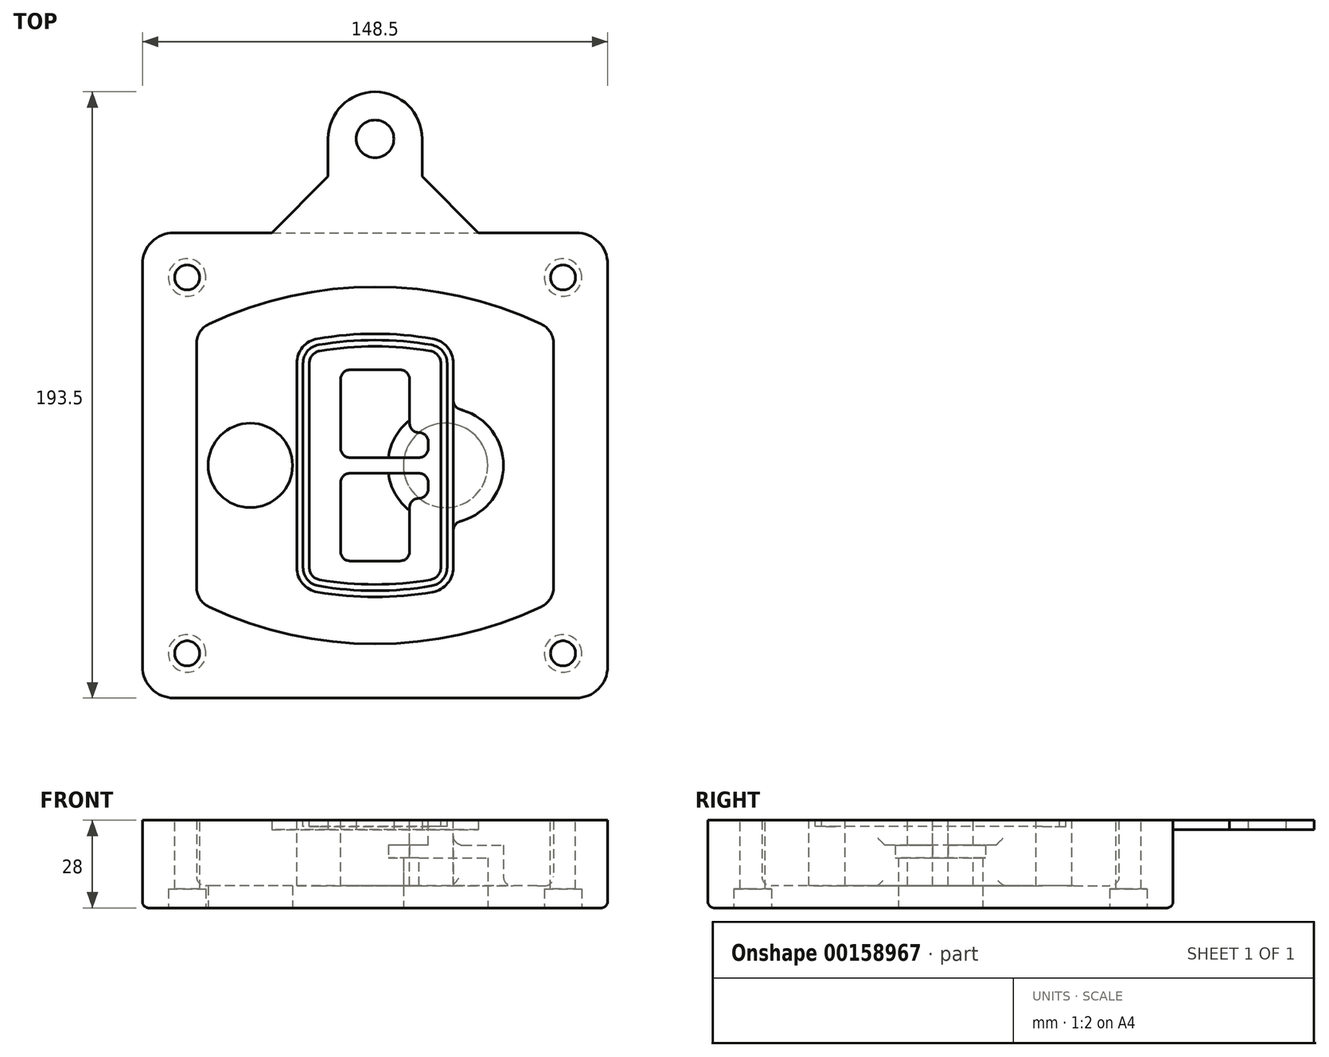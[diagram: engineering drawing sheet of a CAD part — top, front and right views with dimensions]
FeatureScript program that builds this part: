
annotation { "Feature Type Name" : "Feature", "Feature Type Description" : "" }
export const myFeature = defineFeature(function(context is Context, id is Id, definition is map)
    precondition{}
    {
        {
            var Q0;
            Q0=qCreatedBy(makeId("Top.planeOp"),FACE);
            var sketch = newSketch(context, id + "F0", { "sketchPlane" : qUnion([Q0])});
            skPoint(sketch, "E0.rect.middle", {"position": v(0, 0) * mm});
            skLineSegment(sketch, "E1.bottom", {"start": v(-64.25, -74.25) * mm, "end": v(64.25, -74.25) * mm});
            skLineSegment(sketch, "E1.top", {"start": v(-64.25, 74.25) * mm, "end": v(64.25, 74.25) * mm});
            skLineSegment(sketch, "E1.left", {"start": v(-74.25, -64.25) * mm, "end": v(-74.25, 64.25) * mm});
            skLineSegment(sketch, "E1.right", {"start": v(74.25, -64.25) * mm, "end": v(74.25, 64.25) * mm});
            skLineSegment(sketch, "E2", {"start": v(-74.25, 74.25) * mm, "end": v(74.25, -74.25) * mm, "construction": true});
            skLineSegment(sketch, "E3", {"start": v(74.25, 74.25) * mm, "end": v(-74.25, -74.25) * mm, "construction": true});
            skCircle(sketch, "E4", {"center": v(-60, 60) * mm, "radius": 4 * mm});
            skCircle(sketch, "E5", {"center": v(60, 60) * mm, "radius": 4 * mm});
            skCircle(sketch, "E6", {"center": v(60, -60) * mm, "radius": 4 * mm});
            skCircle(sketch, "E7", {"center": v(-60, -60) * mm, "radius": 4 * mm});
            skLineSegment(sketch, "E8", {"start": v(-60, 60) * mm, "end": v(60, 60) * mm, "construction": true});
            skLineSegment(sketch, "E9", {"start": v(60, 60) * mm, "end": v(60, -60) * mm, "construction": true});
            skLineSegment(sketch, "E10", {"start": v(60, -60) * mm, "end": v(-60, -60) * mm, "construction": true});
            skLineSegment(sketch, "E11", {"start": v(-60, -60) * mm, "end": v(-60, 60) * mm, "construction": true});
            skLineSegment(sketch, "E12", {"start": v(-60, 38.83) * mm, "end": v(-60, -38.83) * mm});
            skLineSegment(sketch, "E13", {"start": v(60, 38.83) * mm, "end": v(60, -38.83) * mm});
            skArc(sketch, "E14", {"start": v(54.26, 47.88) * mm, "mid": v(0, 60) * mm, "end": v(-54.26, 47.88) * mm});
            skArc(sketch, "E15", {"start": v(-54.26, -47.88) * mm, "mid": v(0, -60) * mm, "end": v(54.26, -47.88) * mm});
            skLineSegment(sketch, "E16", {"start": v(-60, 0) * mm, "end": v(60, 0) * mm, "construction": true});
            skPoint(sketch, "E17.visualSharp", {"position": v(-60, -45) * mm});
            skArc(sketch, "E17.filletArc", {"start": v(-60, -38.83) * mm, "mid": v(-58.44, -44.2) * mm, "end": v(-54.26, -47.88) * mm});
            skPoint(sketch, "E18.visualSharp", {"position": v(-60, 45) * mm});
            skArc(sketch, "E18.filletArc", {"start": v(-54.26, 47.88) * mm, "mid": v(-58.44, 44.2) * mm, "end": v(-60, 38.83) * mm});
            skPoint(sketch, "E19.visualSharp", {"position": v(60, 45) * mm});
            skArc(sketch, "E19.filletArc", {"start": v(60, 38.83) * mm, "mid": v(58.44, 44.2) * mm, "end": v(54.26, 47.88) * mm});
            skPoint(sketch, "E20.visualSharp", {"position": v(60, -45) * mm});
            skArc(sketch, "E20.filletArc", {"start": v(54.26, -47.88) * mm, "mid": v(58.44, -44.2) * mm, "end": v(60, -38.83) * mm});
            skPoint(sketch, "E21.visualSharp", {"position": v(-74.25, 74.25) * mm});
            skArc(sketch, "E21.filletArc", {"start": v(-64.25, 74.25) * mm, "mid": v(-71.32, 71.32) * mm, "end": v(-74.25, 64.25) * mm});
            skPoint(sketch, "E22.visualSharp", {"position": v(74.25, 74.25) * mm});
            skArc(sketch, "E22.filletArc", {"start": v(74.25, 64.25) * mm, "mid": v(71.32, 71.32) * mm, "end": v(64.25, 74.25) * mm});
            skPoint(sketch, "E23.visualSharp", {"position": v(74.25, -74.25) * mm});
            skArc(sketch, "E23.filletArc", {"start": v(64.25, -74.25) * mm, "mid": v(71.32, -71.32) * mm, "end": v(74.25, -64.25) * mm});
            skPoint(sketch, "E24.visualSharp", {"position": v(-74.25, -74.25) * mm});
            skArc(sketch, "E24.filletArc", {"start": v(-74.25, -64.25) * mm, "mid": v(-71.32, -71.32) * mm, "end": v(-64.25, -74.25) * mm});
            skArc(sketch, "E25.0", {"start": v(57, 38.83) * mm, "mid": v(55.9, 42.58) * mm, "end": v(52.98, 45.17) * mm});
            skLineSegment(sketch, "E25.1", {"start": v(57, 38.83) * mm, "end": v(57, -38.83) * mm});
            skArc(sketch, "E25.2", {"start": v(52.98, -45.17) * mm, "mid": v(55.9, -42.58) * mm, "end": v(57, -38.83) * mm});
            skArc(sketch, "E25.3", {"start": v(-52.98, -45.17) * mm, "mid": v(0, -57) * mm, "end": v(52.98, -45.17) * mm});
            skArc(sketch, "E25.4", {"start": v(-57, -38.83) * mm, "mid": v(-55.9, -42.58) * mm, "end": v(-52.98, -45.17) * mm});
            skArc(sketch, "E25.5", {"start": v(52.98, 45.17) * mm, "mid": v(0, 57) * mm, "end": v(-52.98, 45.17) * mm});
            skLineSegment(sketch, "E25.6", {"start": v(-57, 38.83) * mm, "end": v(-57, -38.83) * mm});
            skArc(sketch, "E25.7", {"start": v(-52.98, 45.17) * mm, "mid": v(-55.9, 42.58) * mm, "end": v(-57, 38.83) * mm});
            skArc(sketch, "E26.0", {"start": v(-55.96, 51.5) * mm, "mid": v(-61.82, 46.33) * mm, "end": v(-64, 38.83) * mm});
            skArc(sketch, "E26.1", {"start": v(55.96, 51.5) * mm, "mid": v(0, 64) * mm, "end": v(-55.96, 51.5) * mm});
            skArc(sketch, "E26.2", {"start": v(64, 38.83) * mm, "mid": v(61.82, 46.33) * mm, "end": v(55.96, 51.5) * mm});
            skLineSegment(sketch, "E26.3", {"start": v(64, 38.83) * mm, "end": v(64, -38.83) * mm});
            skArc(sketch, "E26.4", {"start": v(55.96, -51.5) * mm, "mid": v(61.82, -46.33) * mm, "end": v(64, -38.83) * mm});
            skLineSegment(sketch, "E26.5", {"start": v(-64, 38.83) * mm, "end": v(-64, -38.83) * mm});
            skArc(sketch, "E26.6", {"start": v(-55.96, -51.5) * mm, "mid": v(0, -64) * mm, "end": v(55.96, -51.5) * mm});
            skArc(sketch, "E26.7", {"start": v(-64, -38.83) * mm, "mid": v(-61.82, -46.33) * mm, "end": v(-55.96, -51.5) * mm});
            skSolve(sketch);
        }
        {
            var Q0;
            Q0=makeQuery(id+"F0.imprint","IMPRINT",FACE,{"disambiguationData":[TD([[makeQuery(id+"F0.imprint","IMPRINT",EDGE,{"derivedFrom":sQuery(id+"F0.wireOp",EDGE,"E1.bottom")}),1.0]])]});
            var Q1;
            Q1=makeQuery(id+"F0.imprint","IMPRINT",FACE,{"disambiguationData":[TD([[makeQuery(id+"F0.imprint","IMPRINT",EDGE,{"derivedFrom":sQuery(id+"F0.wireOp",EDGE,"E12")}),1.0]])]});
            var Q2;
            Q2=makeQuery(id+"F0.imprint","IMPRINT",FACE,{"disambiguationData":[TD([[makeQuery(id+"F0.imprint","IMPRINT",EDGE,{"derivedFrom":sQuery(id+"F0.wireOp",EDGE,"E25.0")}),1.0]])]});
            var Q3;
            Q3=makeQuery(id+"F0.imprint","IMPRINT",FACE,{"disambiguationData":[TD([[makeQuery(id+"F0.imprint","IMPRINT",EDGE,{"derivedFrom":sQuery(id+"F0.wireOp",EDGE,"E12")}),-1.0]])]});
            extrude(context, id + "F1", {"entities" : qUnion([Q0, Q1, Q2, Q3]), "oppositeDirection" : true, "depth" : 25 * mm});
        }
        {
            var Q0;
            Q0=makeQuery(id+"F0.imprint","IMPRINT",FACE,{"disambiguationData":[TD([[makeQuery(id+"F0.imprint","IMPRINT",EDGE,{"derivedFrom":sQuery(id+"F0.wireOp",EDGE,"E12")}),1.0]])]});
            extrude(context, id + "F2", {"entities" : qUnion([Q0]), "operationType" : NewBodyOperationType.ADD, "depth" : 3 * mm});
        }
        {
            var Q0;
            Q0=makeQuery(id+"F0.imprint","IMPRINT",FACE,{"disambiguationData":[TD([[makeQuery(id+"F0.imprint","IMPRINT",EDGE,{"derivedFrom":sQuery(id+"F0.wireOp",EDGE,"E25.0")}),1.0]])]});
            extrude(context, id + "F3", {"entities" : qUnion([Q0]), "operationType" : NewBodyOperationType.REMOVE, "oppositeDirection" : true, "depth" : 18 * mm});
        }
        {
            var Q0;
            Q0=makeQuery(id+"F2.opExtrude","CAP_FACE",FACE,{"disambiguationData":[OSD([sQuery(id+"F0.wireOp",EDGE,"E12"),sQuery(id+"F0.wireOp",EDGE,"E13"),sQuery(id+"F0.wireOp",EDGE,"E14"),sQuery(id+"F0.wireOp",EDGE,"E15"),sQuery(id+"F0.wireOp",EDGE,"E17.filletArc"),sQuery(id+"F0.wireOp",EDGE,"E18.filletArc"),sQuery(id+"F0.wireOp",EDGE,"E19.filletArc"),sQuery(id+"F0.wireOp",EDGE,"E20.filletArc"),sQuery(id+"F0.wireOp",EDGE,"E25.0"),sQuery(id+"F0.wireOp",EDGE,"E25.1"),sQuery(id+"F0.wireOp",EDGE,"E25.2"),sQuery(id+"F0.wireOp",EDGE,"E25.3"),sQuery(id+"F0.wireOp",EDGE,"E25.4"),sQuery(id+"F0.wireOp",EDGE,"E25.5"),sQuery(id+"F0.wireOp",EDGE,"E25.6"),sQuery(id+"F0.wireOp",EDGE,"E25.7")])],"isStart":false});
            var sketch = newSketch(context, id + "F4", { "sketchPlane" : qUnion([Q0])});
            skArc(sketch, "E27.0", {"start": v(-18.34, -40.45) * mm, "mid": v(0, -42) * mm, "end": v(18.34, -40.45) * mm});
            skArc(sketch, "E28.0", {"start": v(18.34, 40.45) * mm, "mid": v(0, 42) * mm, "end": v(-18.34, 40.45) * mm});
            skLineSegment(sketch, "E29", {"start": v(-25, 32.57) * mm, "end": v(-25, -32.57) * mm});
            skLineSegment(sketch, "E30", {"start": v(25, 32.57) * mm, "end": v(25, -32.57) * mm});
            skLineSegment(sketch, "E31", {"start": v(-25, 39.1) * mm, "end": v(25, 39.1) * mm, "construction": true});
            skLineSegment(sketch, "E32", {"start": v(-25, -39.1) * mm, "end": v(25, -39.1) * mm, "construction": true});
            skPoint(sketch, "E33.visualSharp", {"position": v(-25, 39.1) * mm});
            skArc(sketch, "E33.filletArc", {"start": v(-18.34, 40.45) * mm, "mid": v(-23.11, 37.73) * mm, "end": v(-25, 32.57) * mm});
            skPoint(sketch, "E34.visualSharp", {"position": v(25, 39.1) * mm});
            skArc(sketch, "E34.filletArc", {"start": v(25, 32.57) * mm, "mid": v(23.11, 37.73) * mm, "end": v(18.34, 40.45) * mm});
            skPoint(sketch, "E35.visualSharp", {"position": v(25, -39.1) * mm});
            skArc(sketch, "E35.filletArc", {"start": v(18.34, -40.45) * mm, "mid": v(23.11, -37.73) * mm, "end": v(25, -32.57) * mm});
            skPoint(sketch, "E36.visualSharp", {"position": v(-25, -39.1) * mm});
            skArc(sketch, "E36.filletArc", {"start": v(-25, -32.57) * mm, "mid": v(-23.11, -37.73) * mm, "end": v(-18.34, -40.45) * mm});
            skArc(sketch, "E37.0", {"start": v(52.98, 45.17) * mm, "mid": v(0, 57) * mm, "end": v(-52.98, 45.17) * mm});
            skArc(sketch, "E37.1", {"start": v(-52.98, 45.17) * mm, "mid": v(-55.9, 42.58) * mm, "end": v(-57, 38.83) * mm});
            skLineSegment(sketch, "E37.2", {"start": v(-57, 38.83) * mm, "end": v(-57, -38.83) * mm});
            skArc(sketch, "E37.3", {"start": v(-57, -38.83) * mm, "mid": v(-55.9, -42.58) * mm, "end": v(-52.98, -45.17) * mm});
            skArc(sketch, "E37.4", {"start": v(-52.98, -45.17) * mm, "mid": v(0, -57) * mm, "end": v(52.98, -45.17) * mm});
            skArc(sketch, "E37.5", {"start": v(52.98, -45.17) * mm, "mid": v(55.9, -42.58) * mm, "end": v(57, -38.83) * mm});
            skLineSegment(sketch, "E37.6", {"start": v(57, 38.83) * mm, "end": v(57, -38.83) * mm});
            skArc(sketch, "E37.7", {"start": v(57, 38.83) * mm, "mid": v(55.9, 42.58) * mm, "end": v(52.98, 45.17) * mm});
            skLineSegment(sketch, "E38.0", {"start": v(23, 32.57) * mm, "end": v(23, -32.57) * mm});
            skArc(sketch, "E38.1", {"start": v(18, -38.48) * mm, "mid": v(21.58, -36.44) * mm, "end": v(23, -32.57) * mm});
            skArc(sketch, "E38.2", {"start": v(-18, -38.48) * mm, "mid": v(0, -40) * mm, "end": v(18, -38.48) * mm});
            skArc(sketch, "E38.3", {"start": v(-23, -32.57) * mm, "mid": v(-21.58, -36.44) * mm, "end": v(-18, -38.48) * mm});
            skLineSegment(sketch, "E38.4", {"start": v(-23, 32.57) * mm, "end": v(-23, -32.57) * mm});
            skArc(sketch, "E38.5", {"start": v(23, 32.57) * mm, "mid": v(21.58, 36.44) * mm, "end": v(18, 38.48) * mm});
            skArc(sketch, "E38.6", {"start": v(-18, 38.48) * mm, "mid": v(-21.58, 36.44) * mm, "end": v(-23, 32.57) * mm});
            skArc(sketch, "E38.7", {"start": v(18, 38.48) * mm, "mid": v(0, 40) * mm, "end": v(-18, 38.48) * mm});
            skArc(sketch, "E39.0", {"start": v(21, 32.57) * mm, "mid": v(20.06, 35.15) * mm, "end": v(17.67, 36.5) * mm});
            skLineSegment(sketch, "E39.1", {"start": v(21, 32.57) * mm, "end": v(21, -32.57) * mm});
            skArc(sketch, "E39.2", {"start": v(17.67, -36.5) * mm, "mid": v(20.06, -35.15) * mm, "end": v(21, -32.57) * mm});
            skArc(sketch, "E39.3", {"start": v(-17.67, -36.5) * mm, "mid": v(0, -38) * mm, "end": v(17.67, -36.5) * mm});
            skArc(sketch, "E39.4", {"start": v(-21, -32.57) * mm, "mid": v(-20.06, -35.15) * mm, "end": v(-17.67, -36.5) * mm});
            skArc(sketch, "E39.5", {"start": v(17.67, 36.5) * mm, "mid": v(0, 38) * mm, "end": v(-17.67, 36.5) * mm});
            skLineSegment(sketch, "E39.6", {"start": v(-21, 32.57) * mm, "end": v(-21, -32.57) * mm});
            skArc(sketch, "E39.7", {"start": v(-17.67, 36.5) * mm, "mid": v(-20.06, 35.15) * mm, "end": v(-21, 32.57) * mm});
            skLineSegment(sketch, "E40", {"start": v(-25, 0) * mm, "end": v(25, 0) * mm, "construction": true});
            skLineSegment(sketch, "E41", {"start": v(-11, 5.5) * mm, "end": v(-11, 27.5) * mm});
            skLineSegment(sketch, "E42", {"start": v(-8, 30.5) * mm, "end": v(8, 30.5) * mm});
            skLineSegment(sketch, "E43", {"start": v(11, 27.5) * mm, "end": v(11, 13.5) * mm});
            skLineSegment(sketch, "E44", {"start": v(14, 10.5) * mm, "end": v(14, 10.5) * mm});
            skLineSegment(sketch, "E45", {"start": v(17, 7.5) * mm, "end": v(17, 5.5) * mm});
            skLineSegment(sketch, "E46", {"start": v(14, 2.5) * mm, "end": v(-8, 2.5) * mm});
            skPoint(sketch, "E47.visualSharp", {"position": v(-11, 30.5) * mm});
            skArc(sketch, "E47.filletArc", {"start": v(-8, 30.5) * mm, "mid": v(-10.12, 29.62) * mm, "end": v(-11, 27.5) * mm});
            skPoint(sketch, "E48.visualSharp", {"position": v(11, 30.5) * mm});
            skArc(sketch, "E48.filletArc", {"start": v(11, 27.5) * mm, "mid": v(10.12, 29.62) * mm, "end": v(8, 30.5) * mm});
            skPoint(sketch, "E49.visualSharp", {"position": v(11, 10.5) * mm});
            skArc(sketch, "E49.filletArc", {"start": v(11, 13.5) * mm, "mid": v(11.88, 11.38) * mm, "end": v(14, 10.5) * mm});
            skPoint(sketch, "E50.visualSharp", {"position": v(17, 10.5) * mm});
            skArc(sketch, "E50.filletArc", {"start": v(17, 7.5) * mm, "mid": v(16.12, 9.62) * mm, "end": v(14, 10.5) * mm});
            skPoint(sketch, "E51.visualSharp", {"position": v(17, 2.5) * mm});
            skArc(sketch, "E51.filletArc", {"start": v(14, 2.5) * mm, "mid": v(16.12, 3.38) * mm, "end": v(17, 5.5) * mm});
            skPoint(sketch, "E52.visualSharp", {"position": v(-11, 2.5) * mm});
            skArc(sketch, "E52.filletArc", {"start": v(-11, 5.5) * mm, "mid": v(-10.12, 3.38) * mm, "end": v(-8, 2.5) * mm});
            skLineSegment(sketch, "E53.0.MirrorCS", {"start": v(14, -2.5) * mm, "end": v(-8, -2.5) * mm});
            skArc(sketch, "E54.0.MirrorCS", {"start": v(-11, -5.5) * mm, "mid": v(-10.12, -3.38) * mm, "end": v(-8, -2.5) * mm});
            skLineSegment(sketch, "E55.0.MirrorCS", {"start": v(-11, -5.5) * mm, "end": v(-11, -27.5) * mm});
            skArc(sketch, "E56.0.MirrorCS", {"start": v(-8, -30.5) * mm, "mid": v(-10.12, -29.62) * mm, "end": v(-11, -27.5) * mm});
            skLineSegment(sketch, "E57.0.MirrorCS", {"start": v(-8, -30.5) * mm, "end": v(8, -30.5) * mm});
            skArc(sketch, "E58.0.MirrorCS", {"start": v(11, -27.5) * mm, "mid": v(10.12, -29.62) * mm, "end": v(8, -30.5) * mm});
            skLineSegment(sketch, "E59.0.MirrorCS", {"start": v(11, -27.5) * mm, "end": v(11, -13.5) * mm});
            skArc(sketch, "E60.0.MirrorCS", {"start": v(11, -13.5) * mm, "mid": v(11.88, -11.38) * mm, "end": v(14, -10.5) * mm});
            skArc(sketch, "E61.0.MirrorCS", {"start": v(17, -7.5) * mm, "mid": v(16.12, -9.62) * mm, "end": v(14, -10.5) * mm});
            skLineSegment(sketch, "E62.0.MirrorCS", {"start": v(17, -7.5) * mm, "end": v(17, -5.5) * mm});
            skArc(sketch, "E63.0.MirrorCS", {"start": v(14, -2.5) * mm, "mid": v(16.12, -3.38) * mm, "end": v(17, -5.5) * mm});
            skSolve(sketch);
        }
        {
            var Q0;
            Q0=makeQuery(id+"F4.imprint","IMPRINT",FACE,{"disambiguationData":[TD([[makeQuery(id+"F4.imprint","IMPRINT",EDGE,{"derivedFrom":sQuery(id+"F4.wireOp",EDGE,"E27.0")}),1.0]])]});
            var Q1;
            Q1=makeQuery(id+"F4.imprint","IMPRINT",FACE,{"disambiguationData":[TD([[makeQuery(id+"F4.imprint","IMPRINT",EDGE,{"derivedFrom":sQuery(id+"F4.wireOp",EDGE,"E38.0")}),-1.0]])]});
            var Q2;
            Q2=makeQuery(id+"F4.imprint","IMPRINT",FACE,{"disambiguationData":[TD([[makeQuery(id+"F4.imprint","IMPRINT",EDGE,{"derivedFrom":sQuery(id+"F4.wireOp",EDGE,"E39.0")}),1.0]])]});
            extrude(context, id + "F5", {"entities" : qUnion([Q0, Q1, Q2]), "operationType" : NewBodyOperationType.ADD, "endBound" : BoundingType.UP_TO_NEXT, "oppositeDirection" : true, "depth" : 25 * mm});
        }
        {
            var Q0;
            Q0=makeQuery(id+"F4.imprint","IMPRINT",FACE,{"disambiguationData":[TD([[makeQuery(id+"F4.imprint","IMPRINT",EDGE,{"derivedFrom":sQuery(id+"F4.wireOp",EDGE,"E38.0")}),-1.0]])]});
            extrude(context, id + "F6", {"entities" : qUnion([Q0]), "operationType" : NewBodyOperationType.REMOVE, "oppositeDirection" : true, "depth" : 2 * mm});
        }
        {
            var Q0;
            Q0=makeQuery(id+"F1.opExtrude","CAP_FACE",FACE,{"disambiguationData":[OSD([sQuery(id+"F0.wireOp",EDGE,"E1.bottom"),sQuery(id+"F0.wireOp",EDGE,"E1.top"),sQuery(id+"F0.wireOp",EDGE,"E1.left"),sQuery(id+"F0.wireOp",EDGE,"E1.right"),sQuery(id+"F0.wireOp",EDGE,"E4"),sQuery(id+"F0.wireOp",EDGE,"E5"),sQuery(id+"F0.wireOp",EDGE,"E6"),sQuery(id+"F0.wireOp",EDGE,"E7"),sQuery(id+"F0.wireOp",EDGE,"E21.filletArc"),sQuery(id+"F0.wireOp",EDGE,"E22.filletArc"),sQuery(id+"F0.wireOp",EDGE,"E23.filletArc"),sQuery(id+"F0.wireOp",EDGE,"E24.filletArc")])],"isStart":false});
            var sketch = newSketch(context, id + "F7", { "sketchPlane" : qUnion([Q0])});
            skCircle(sketch, "E64", {"center": v(22.5, 0) * mm, "radius": 13.47 * mm});
            skCircle(sketch, "E65", {"center": v(-39.81, 0) * mm, "radius": 13.47 * mm});
            skLineSegment(sketch, "E66", {"start": v(74.25, 0) * mm, "end": v(-74.25, 0) * mm});
            skCircle(sketch, "E67", {"center": v(22.5, 0) * mm, "radius": 18.47 * mm});
            skCircle(sketch, "E68", {"center": v(60, -60) * mm, "radius": 6 * mm});
            skCircle(sketch, "E69", {"center": v(-60, -60) * mm, "radius": 6 * mm});
            skCircle(sketch, "E70", {"center": v(-60, 60) * mm, "radius": 6 * mm});
            skCircle(sketch, "E71", {"center": v(60, 60) * mm, "radius": 6 * mm});
            skSolve(sketch);
        }
        {
            var Q0;
            {var subQ1=sQuery(id+"F7.wireOp",EDGE,"E66");var subQ4=sQuery(id+"F7.wireOp",EDGE,"E64");var subQ6=makeQuery(id+"F7.imprint","INTERSECT",VERTEX,{"disambiguationData":[OD(0.0)],"derivedFrom":[subQ4,subQ1]});Q0=makeQuery(id+"F7.imprint","IMPRINT",FACE,{"disambiguationData":[TD([[makeQuery(id+"F7.imprint","IMPRINT",EDGE,{"disambiguationData":[TD([[subQ6,-1.0]])],"derivedFrom":subQ4}),-1.0]])]});}
            var Q1;
            {var subQ0=sQuery(id+"F7.wireOp",EDGE,"E66");var subQ1=sQuery(id+"F7.wireOp",EDGE,"E64");var subQ3=makeQuery(id+"F7.imprint","INTERSECT",VERTEX,{"disambiguationData":[OD(0.0)],"derivedFrom":[subQ1,subQ0]});Q1=makeQuery(id+"F7.imprint","IMPRINT",FACE,{"disambiguationData":[TD([[makeQuery(id+"F7.imprint","IMPRINT",EDGE,{"disambiguationData":[TD([[subQ3,-1.0]])],"derivedFrom":subQ1}),1.0]])]});}
            var Q2;
            {var subQ0=sQuery(id+"F7.wireOp",EDGE,"E66");var subQ1=sQuery(id+"F7.wireOp",EDGE,"E64");var subQ3=makeQuery(id+"F7.imprint","INTERSECT",VERTEX,{"disambiguationData":[OD(0.0)],"derivedFrom":[subQ1,subQ0]});Q2=makeQuery(id+"F7.imprint","IMPRINT",FACE,{"disambiguationData":[TD([[makeQuery(id+"F7.imprint","IMPRINT",EDGE,{"disambiguationData":[TD([[subQ3,1.0]])],"derivedFrom":subQ1}),1.0]])]});}
            var Q3;
            {var subQ1=sQuery(id+"F7.wireOp",EDGE,"E66");var subQ4=sQuery(id+"F7.wireOp",EDGE,"E64");var subQ6=makeQuery(id+"F7.imprint","INTERSECT",VERTEX,{"disambiguationData":[OD(0.0)],"derivedFrom":[subQ4,subQ1]});Q3=makeQuery(id+"F7.imprint","IMPRINT",FACE,{"disambiguationData":[TD([[makeQuery(id+"F7.imprint","IMPRINT",EDGE,{"disambiguationData":[TD([[subQ6,1.0]])],"derivedFrom":subQ4}),-1.0]])]});}
            extrude(context, id + "F8", {"entities" : qUnion([Q0, Q1, Q2, Q3]), "operationType" : NewBodyOperationType.ADD, "oppositeDirection" : true, "depth" : 20 * mm});
        }
        {
            var Q0;
            {var subQ0=sQuery(id+"F7.wireOp",EDGE,"E66");var subQ1=sQuery(id+"F7.wireOp",EDGE,"E64");var subQ3=makeQuery(id+"F7.imprint","INTERSECT",VERTEX,{"disambiguationData":[OD(0.0)],"derivedFrom":[subQ1,subQ0]});Q0=makeQuery(id+"F7.imprint","IMPRINT",FACE,{"disambiguationData":[TD([[makeQuery(id+"F7.imprint","IMPRINT",EDGE,{"disambiguationData":[TD([[subQ3,-1.0]])],"derivedFrom":subQ1}),1.0]])]});}
            var Q1;
            {var subQ0=sQuery(id+"F7.wireOp",EDGE,"E66");var subQ1=sQuery(id+"F7.wireOp",EDGE,"E64");var subQ3=makeQuery(id+"F7.imprint","INTERSECT",VERTEX,{"disambiguationData":[OD(0.0)],"derivedFrom":[subQ1,subQ0]});Q1=makeQuery(id+"F7.imprint","IMPRINT",FACE,{"disambiguationData":[TD([[makeQuery(id+"F7.imprint","IMPRINT",EDGE,{"disambiguationData":[TD([[subQ3,1.0]])],"derivedFrom":subQ1}),1.0]])]});}
            extrude(context, id + "F9", {"entities" : qUnion([Q0, Q1]), "operationType" : NewBodyOperationType.REMOVE, "oppositeDirection" : true, "depth" : 16 * mm});
        }
        {
            var Q0;
            {var subQ0=sQuery(id+"F7.wireOp",EDGE,"E66");var subQ1=sQuery(id+"F7.wireOp",EDGE,"E65");var subQ3=makeQuery(id+"F7.imprint","INTERSECT",VERTEX,{"disambiguationData":[OD(0.0)],"derivedFrom":[subQ1,subQ0]});Q0=makeQuery(id+"F7.imprint","IMPRINT",FACE,{"disambiguationData":[TD([[makeQuery(id+"F7.imprint","IMPRINT",EDGE,{"disambiguationData":[TD([[subQ3,-1.0]])],"derivedFrom":subQ1}),1.0]])]});}
            var Q1;
            {var subQ0=sQuery(id+"F7.wireOp",EDGE,"E66");var subQ1=sQuery(id+"F7.wireOp",EDGE,"E65");var subQ3=makeQuery(id+"F7.imprint","INTERSECT",VERTEX,{"disambiguationData":[OD(0.0)],"derivedFrom":[subQ1,subQ0]});Q1=makeQuery(id+"F7.imprint","IMPRINT",FACE,{"disambiguationData":[TD([[makeQuery(id+"F7.imprint","IMPRINT",EDGE,{"disambiguationData":[TD([[subQ3,1.0]])],"derivedFrom":subQ1}),1.0]])]});}
            extrude(context, id + "F10", {"entities" : qUnion([Q0, Q1]), "operationType" : NewBodyOperationType.REMOVE, "oppositeDirection" : true, "depth" : 25 * mm});
        }
        {
            var Q0;
            Q0=makeQuery(id+"F7.imprint","IMPRINT",FACE,{"disambiguationData":[TD([[makeQuery(id+"F7.imprint","IMPRINT",EDGE,{"derivedFrom":sQuery(id+"F7.wireOp",EDGE,"E68")}),1.0]])]});
            var Q1;
            Q1=makeQuery(id+"F7.imprint","IMPRINT",FACE,{"disambiguationData":[TD([[makeQuery(id+"F7.imprint","IMPRINT",EDGE,{"derivedFrom":makeQuery(id+"F1.opExtrude","CAP_EDGE",EDGE,{"disambiguationData":[OSD([sQuery(id+"F0.wireOp",EDGE,"E5")])],"isStart":false})}),-1.0]])]});
            var Q2;
            Q2=makeQuery(id+"F7.imprint","IMPRINT",FACE,{"disambiguationData":[TD([[makeQuery(id+"F7.imprint","IMPRINT",EDGE,{"derivedFrom":sQuery(id+"F7.wireOp",EDGE,"E69")}),1.0]])]});
            var Q3;
            Q3=makeQuery(id+"F7.imprint","IMPRINT",FACE,{"disambiguationData":[TD([[makeQuery(id+"F7.imprint","IMPRINT",EDGE,{"derivedFrom":makeQuery(id+"F1.opExtrude","CAP_EDGE",EDGE,{"disambiguationData":[OSD([sQuery(id+"F0.wireOp",EDGE,"E4")])],"isStart":false})}),-1.0]])]});
            var Q4;
            Q4=makeQuery(id+"F7.imprint","IMPRINT",FACE,{"disambiguationData":[TD([[makeQuery(id+"F7.imprint","IMPRINT",EDGE,{"derivedFrom":sQuery(id+"F7.wireOp",EDGE,"E70")}),1.0]])]});
            var Q5;
            Q5=makeQuery(id+"F7.imprint","IMPRINT",FACE,{"disambiguationData":[TD([[makeQuery(id+"F7.imprint","IMPRINT",EDGE,{"derivedFrom":makeQuery(id+"F1.opExtrude","CAP_EDGE",EDGE,{"disambiguationData":[OSD([sQuery(id+"F0.wireOp",EDGE,"E7")])],"isStart":false})}),-1.0]])]});
            var Q6;
            Q6=makeQuery(id+"F7.imprint","IMPRINT",FACE,{"disambiguationData":[TD([[makeQuery(id+"F7.imprint","IMPRINT",EDGE,{"derivedFrom":sQuery(id+"F7.wireOp",EDGE,"E71")}),1.0]])]});
            var Q7;
            Q7=makeQuery(id+"F7.imprint","IMPRINT",FACE,{"disambiguationData":[TD([[makeQuery(id+"F7.imprint","IMPRINT",EDGE,{"derivedFrom":makeQuery(id+"F1.opExtrude","CAP_EDGE",EDGE,{"disambiguationData":[OSD([sQuery(id+"F0.wireOp",EDGE,"E6")])],"isStart":false})}),-1.0]])]});
            extrude(context, id + "F11", {"entities" : qUnion([Q0, Q1, Q2, Q3, Q4, Q5, Q6, Q7]), "operationType" : NewBodyOperationType.REMOVE, "oppositeDirection" : true, "depth" : 6 * mm});
        }
        {
            var Q0;
            Q0=makeQuery(id+"F9.boolean.opBoolean","COPY",FACE,{"derivedFrom":makeQuery(id+"F9.opExtrude","CAP_FACE",FACE,{"disambiguationData":[OSD([sQuery(id+"F7.wireOp",EDGE,"E64")])],"isStart":false})});
            var sketch = newSketch(context, id + "F12", { "sketchPlane" : qUnion([Q0])});
            skArc(sketch, "E72.0", {"start": v(11, 14.45) * mm, "mid": v(6.45, 9.13) * mm, "end": v(4.2, 2.5) * mm});
            skArc(sketch, "E72.1", {"start": v(4.2, -2.5) * mm, "mid": v(6.45, -9.13) * mm, "end": v(11, -14.45) * mm});
            skLineSegment(sketch, "E73", {"start": v(4.2, -2.5) * mm, "end": v(14, -2.5) * mm});
            skLineSegment(sketch, "E74.0", {"start": v(14, 2.5) * mm, "end": v(4.2, 2.5) * mm});
            skArc(sketch, "E74.1", {"start": v(14, 2.5) * mm, "mid": v(16.12, 3.38) * mm, "end": v(17, 5.5) * mm});
            skLineSegment(sketch, "E74.2", {"start": v(17, 7.5) * mm, "end": v(17, 5.5) * mm});
            skArc(sketch, "E74.3", {"start": v(17, 7.5) * mm, "mid": v(16.12, 9.62) * mm, "end": v(14, 10.5) * mm});
            skArc(sketch, "E74.4", {"start": v(11, 13.5) * mm, "mid": v(11.88, 11.38) * mm, "end": v(14, 10.5) * mm});
            skLineSegment(sketch, "E74.5", {"start": v(11, 14.45) * mm, "end": v(11, 13.5) * mm});
            skLineSegment(sketch, "E74.7", {"start": v(14, -2.5) * mm, "end": v(4.2, -2.5) * mm});
            skArc(sketch, "E74.8", {"start": v(14, -2.5) * mm, "mid": v(16.12, -3.38) * mm, "end": v(17, -5.5) * mm});
            skLineSegment(sketch, "E74.9", {"start": v(17, -7.5) * mm, "end": v(17, -5.5) * mm});
            skArc(sketch, "E74.10", {"start": v(17, -7.5) * mm, "mid": v(16.12, -9.62) * mm, "end": v(14, -10.5) * mm});
            skArc(sketch, "E74.11", {"start": v(11, -13.5) * mm, "mid": v(11.88, -11.38) * mm, "end": v(14, -10.5) * mm});
            skLineSegment(sketch, "E74.12", {"start": v(11, -14.45) * mm, "end": v(11, -13.5) * mm});
            skPoint(sketch, "E75.orphan", {"position": v(11, -27.5) * mm});
            skPoint(sketch, "E76.orphan", {"position": v(-8, -2.5) * mm});
            skPoint(sketch, "E77.orphan", {"position": v(-8, 2.5) * mm});
            skPoint(sketch, "E78.orphan", {"position": v(11, 27.5) * mm});
            skSolve(sketch);
        }
        {
            var Q0;
            {var subQ7=sQuery(id+"F12.wireOp",EDGE,"E72.0");var subQ14=sQuery(id+"F12.wireOp",EDGE,"E72.1");var subQ16=sQuery(id+"F12.wireOp",EDGE,"E74.1");var subQ18=sQuery(id+"F12.wireOp",EDGE,"E74.8");Q0=qUnion([makeQuery(id+"F12.imprint","IMPRINT",FACE,{"disambiguationData":[TD([[makeQuery(id+"F12.imprint","IMPRINT",EDGE,{"derivedFrom":subQ7}),1.0]])]}),makeQuery(id+"F12.imprint","IMPRINT",FACE,{"disambiguationData":[TD([[makeQuery(id+"F12.imprint","IMPRINT",EDGE,{"derivedFrom":subQ14}),1.0]])]}),makeQuery(id+"F12.imprint","IMPRINT",FACE,{"disambiguationData":[TD([[makeQuery(id+"F12.imprint","IMPRINT",EDGE,{"derivedFrom":subQ16}),1.0]])]}),makeQuery(id+"F12.imprint","IMPRINT",FACE,{"disambiguationData":[TD([[makeQuery(id+"F12.imprint","IMPRINT",EDGE,{"derivedFrom":subQ18}),-1.0]])]})]);}
            var Q1;
            Q1=makeQuery(id+"F5.boolean.opBoolean","SPLIT",FACE,{"disambiguationData":[TD([makeQuery(id+"F5.opExtrude","SWEPT_FACE",FACE,{"disambiguationData":[OSD([sQuery(id+"F4.wireOp",EDGE,"E41")])]})])],"derivedFrom":makeQuery(id+"F3.boolean.opBoolean","COPY",FACE,{"derivedFrom":makeQuery(id+"F3.opExtrude","CAP_FACE",FACE,{"disambiguationData":[OSD([sQuery(id+"F0.wireOp",EDGE,"E25.0"),sQuery(id+"F0.wireOp",EDGE,"E25.1"),sQuery(id+"F0.wireOp",EDGE,"E25.2"),sQuery(id+"F0.wireOp",EDGE,"E25.3"),sQuery(id+"F0.wireOp",EDGE,"E25.4"),sQuery(id+"F0.wireOp",EDGE,"E25.5"),sQuery(id+"F0.wireOp",EDGE,"E25.6"),sQuery(id+"F0.wireOp",EDGE,"E25.7")])],"isStart":false})})});
            extrude(context, id + "F13", {"entities" : qUnion([Q0]), "operationType" : NewBodyOperationType.REMOVE, "endBound" : BoundingType.UP_TO_SURFACE, "endBoundEntityFace" : qUnion([Q1]), "depth" : 25 * mm});
        }
        {
            var Q0;
            Q0=makeQuery(id+"F3.boolean.opBoolean","COPY",EDGE,{"derivedFrom":makeQuery(id+"F3.opExtrude","CAP_EDGE",EDGE,{"disambiguationData":[OSD([sQuery(id+"F0.wireOp",EDGE,"E25.6")])],"isStart":false})});
            var Q1;
            Q1=makeQuery(id+"F8.boolean.opBoolean","INTERSECT",EDGE,{"derivedFrom":[makeQuery(id+"F5.opExtrude","SWEPT_FACE",FACE,{"disambiguationData":[OSD([sQuery(id+"F4.wireOp",EDGE,"E30")])]}),makeQuery(id+"F8.opExtrude","CAP_FACE",FACE,{"disambiguationData":[OSD([sQuery(id+"F7.wireOp",EDGE,"E67")])],"isStart":false})]});
            var Q2;
            Q2=makeQuery(id+"F8.boolean.opBoolean","INTERSECT",EDGE,{"disambiguationData":[OD(1.0)],"derivedFrom":[makeQuery(id+"F5.opExtrude","SWEPT_FACE",FACE,{"disambiguationData":[OSD([sQuery(id+"F4.wireOp",EDGE,"E30")])]}),makeQuery(id+"F8.opExtrude","SWEPT_FACE",FACE,{"disambiguationData":[OSD([sQuery(id+"F7.wireOp",EDGE,"E67")])]})]});
            var Q3;
            {var subQ0=sQuery(id+"F4.wireOp",EDGE,"E30");Q3=makeQuery(id+"F8.boolean.opBoolean","SPLIT",EDGE,{"disambiguationData":[TD([makeQuery(id+"F5.opExtrude","SWEPT_FACE",FACE,{"disambiguationData":[OSD([sQuery(id+"F4.wireOp",EDGE,"E35.filletArc")])]})])],"derivedFrom":makeQuery(id+"F5.opExtrude","CAP_EDGE",EDGE,{"disambiguationData":[OSD([subQ0])],"isStart":false})});}
            var Q4;
            {var subQ0=sQuery(id+"F0.wireOp",EDGE,"E25.7");var subQ1=sQuery(id+"F0.wireOp",EDGE,"E25.1");var subQ2=sQuery(id+"F0.wireOp",EDGE,"E25.6");var subQ3=sQuery(id+"F0.wireOp",EDGE,"E25.5");var subQ4=sQuery(id+"F0.wireOp",EDGE,"E25.4");var subQ5=sQuery(id+"F0.wireOp",EDGE,"E25.0");var subQ6=sQuery(id+"F0.wireOp",EDGE,"E25.2");var subQ7=sQuery(id+"F0.wireOp",EDGE,"E25.3");Q4=makeQuery(id+"F8.boolean.opBoolean","INTERSECT",EDGE,{"derivedFrom":[makeQuery(id+"F5.boolean.opBoolean","SPLIT",FACE,{"disambiguationData":[TD([makeQuery(id+"F2.opExtrude","SWEPT_FACE",FACE,{"disambiguationData":[OSD([subQ5])]})])],"derivedFrom":makeQuery(id+"F3.boolean.opBoolean","COPY",FACE,{"derivedFrom":makeQuery(id+"F3.opExtrude","CAP_FACE",FACE,{"disambiguationData":[OSD([subQ5,subQ1,subQ6,subQ7,subQ4,subQ3,subQ2,subQ0])],"isStart":false})})}),makeQuery(id+"F8.opExtrude","SWEPT_FACE",FACE,{"disambiguationData":[OSD([sQuery(id+"F7.wireOp",EDGE,"E67")])]})]});}
            var Q5;
            Q5=makeQuery(id+"F8.boolean.opBoolean","INTERSECT",EDGE,{"disambiguationData":[OD(0.0)],"derivedFrom":[makeQuery(id+"F5.opExtrude","SWEPT_FACE",FACE,{"disambiguationData":[OSD([sQuery(id+"F4.wireOp",EDGE,"E30")])]}),makeQuery(id+"F8.opExtrude","SWEPT_FACE",FACE,{"disambiguationData":[OSD([sQuery(id+"F7.wireOp",EDGE,"E67")])]})]});
            fillet(context, id + "F14", {"entities" : qUnion([Q0, Q1, Q2, Q3, Q4, Q5]), "radius" : 3 * mm, "tangentPropagation" : true, "allowEdgeOverflow" : false});
        }
        {
            var Q0;
            Q0=makeQuery(id+"F1.opExtrude","CAP_EDGE",EDGE,{"disambiguationData":[OSD([sQuery(id+"F0.wireOp",EDGE,"E1.bottom")])],"isStart":false});
            fillet(context, id + "F15", {"entities" : qUnion([Q0]), "radius" : 2 * mm, "tangentPropagation" : true, "allowEdgeOverflow" : false});
        }
        {
            var Q0;
            {var subQ0=sQuery(id+"F0.wireOp",EDGE,"E22.filletArc");var subQ1=sQuery(id+"F0.wireOp",EDGE,"E7");var subQ2=sQuery(id+"F0.wireOp",EDGE,"E6");var subQ3=sQuery(id+"F0.wireOp",EDGE,"E5");var subQ4=sQuery(id+"F0.wireOp",EDGE,"E4");var subQ5=sQuery(id+"F0.wireOp",EDGE,"E1.bottom");var subQ6=sQuery(id+"F0.wireOp",EDGE,"E21.filletArc");var subQ7=sQuery(id+"F0.wireOp",EDGE,"E1.top");var subQ8=sQuery(id+"F0.wireOp",EDGE,"E1.left");var subQ9=sQuery(id+"F0.wireOp",EDGE,"E1.right");var subQ10=sQuery(id+"F0.wireOp",EDGE,"E23.filletArc");var subQ11=sQuery(id+"F0.wireOp",EDGE,"E24.filletArc");Q0=makeQuery(id+"F2.boolean.opBoolean","SPLIT",FACE,{"disambiguationData":[TD([makeQuery(id+"F1.opExtrude","SWEPT_FACE",FACE,{"disambiguationData":[OSD([subQ5])]})])],"derivedFrom":makeQuery(id+"F1.opExtrude","CAP_FACE",FACE,{"disambiguationData":[OSD([subQ5,subQ7,subQ8,subQ9,subQ4,subQ3,subQ2,subQ1,subQ6,subQ0,subQ10,subQ11])],"isStart":true})});}
            var sketch = newSketch(context, id + "F16", { "sketchPlane" : qUnion([Q0])});
            skLineSegment(sketch, "E79", {"start": v(0, 74.25) * mm, "end": v(0, 104.25) * mm, "construction": true});
            skPoint(sketch, "E79.endSnap0", {"position": v(0, 74.25) * mm});
            skCircle(sketch, "E80", {"center": v(0, 104.25) * mm, "radius": 6 * mm});
            skArc(sketch, "E81", {"start": v(15, 104.25) * mm, "mid": v(0, 119.25) * mm, "end": v(-15, 104.25) * mm});
            skLineSegment(sketch, "E82", {"start": v(-15, 104.25) * mm, "end": v(-15, 92.25) * mm});
            skLineSegment(sketch, "E83", {"start": v(-15, 92.25) * mm, "end": v(-33, 74.25) * mm});
            skLineSegment(sketch, "E84", {"start": v(33, 74.25) * mm, "end": v(15, 92.25) * mm});
            skLineSegment(sketch, "E85", {"start": v(15, 92.25) * mm, "end": v(15, 104.25) * mm});
            skLineSegment(sketch, "E86", {"start": v(-74.25, 0) * mm, "end": v(74.25, 0) * mm});
            skArc(sketch, "E87.MirrorCS", {"start": v(15, -104.25) * mm, "mid": v(0, -119.25) * mm, "end": v(-15, -104.25) * mm});
            skCircle(sketch, "E88.MirrorC", {"center": v(0, -104.25) * mm, "radius": 6 * mm});
            skLineSegment(sketch, "E89.MirrorCS", {"start": v(15, -92.25) * mm, "end": v(15, -104.25) * mm});
            skLineSegment(sketch, "E90.MirrorCS", {"start": v(33, -74.25) * mm, "end": v(15, -92.25) * mm});
            skLineSegment(sketch, "E91.MirrorCS", {"start": v(-15, -92.25) * mm, "end": v(-33, -74.25) * mm});
            skLineSegment(sketch, "E92.MirrorCS", {"start": v(-15, -104.25) * mm, "end": v(-15, -92.25) * mm});
            skSolve(sketch);
        }
        {
            var Q0;
            Q0=makeQuery(id+"F16.imprint","IMPRINT",FACE,{"disambiguationData":[TD([[makeQuery(id+"F16.imprint","IMPRINT",EDGE,{"derivedFrom":sQuery(id+"F16.wireOp",EDGE,"E80")}),-1.0]])]});
            var Q1;
            Q1=makeQuery(id+"F16.imprint","IMPRINT",FACE,{"disambiguationData":[TD([[makeQuery(id+"F16.imprint","IMPRINT",EDGE,{"derivedFrom":makeQuery(id+"F1.opExtrude","CAP_EDGE",EDGE,{"disambiguationData":[OSD([sQuery(id+"F0.wireOp",EDGE,"E4")])],"isStart":true})}),-1.0]])]});
            var Q2;
            Q2=makeQuery(id+"F16.imprint","IMPRINT",FACE,{"disambiguationData":[TD([[makeQuery(id+"F16.imprint","IMPRINT",EDGE,{"derivedFrom":makeQuery(id+"F1.opExtrude","CAP_EDGE",EDGE,{"disambiguationData":[OSD([sQuery(id+"F0.wireOp",EDGE,"E6")])],"isStart":true})}),-1.0]])]});
            var Q3;
            Q3=makeQuery(id+"F16.imprint","IMPRINT",FACE,{"disambiguationData":[TD([[makeQuery(id+"F16.imprint","IMPRINT",EDGE,{"derivedFrom":sQuery(id+"F16.wireOp",EDGE,"E87.MirrorCS")}),-1.0]])]});
            var Q4;
            Q4=makeQuery(id+"F2.opExtrude","CAP_FACE",FACE,{"disambiguationData":[OSD([sQuery(id+"F0.wireOp",EDGE,"E12"),sQuery(id+"F0.wireOp",EDGE,"E13"),sQuery(id+"F0.wireOp",EDGE,"E14"),sQuery(id+"F0.wireOp",EDGE,"E15"),sQuery(id+"F0.wireOp",EDGE,"E17.filletArc"),sQuery(id+"F0.wireOp",EDGE,"E18.filletArc"),sQuery(id+"F0.wireOp",EDGE,"E19.filletArc"),sQuery(id+"F0.wireOp",EDGE,"E20.filletArc"),sQuery(id+"F0.wireOp",EDGE,"E25.0"),sQuery(id+"F0.wireOp",EDGE,"E25.1"),sQuery(id+"F0.wireOp",EDGE,"E25.2"),sQuery(id+"F0.wireOp",EDGE,"E25.3"),sQuery(id+"F0.wireOp",EDGE,"E25.4"),sQuery(id+"F0.wireOp",EDGE,"E25.5"),sQuery(id+"F0.wireOp",EDGE,"E25.6"),sQuery(id+"F0.wireOp",EDGE,"E25.7")])],"isStart":false});
            extrude(context, id + "F17", {"entities" : qUnion([Q0, Q1, Q2, Q3]), "operationType" : NewBodyOperationType.ADD, "endBound" : BoundingType.UP_TO_SURFACE, "endBoundEntityFace" : qUnion([Q4]), "depth" : 25 * mm});
        }
    });
